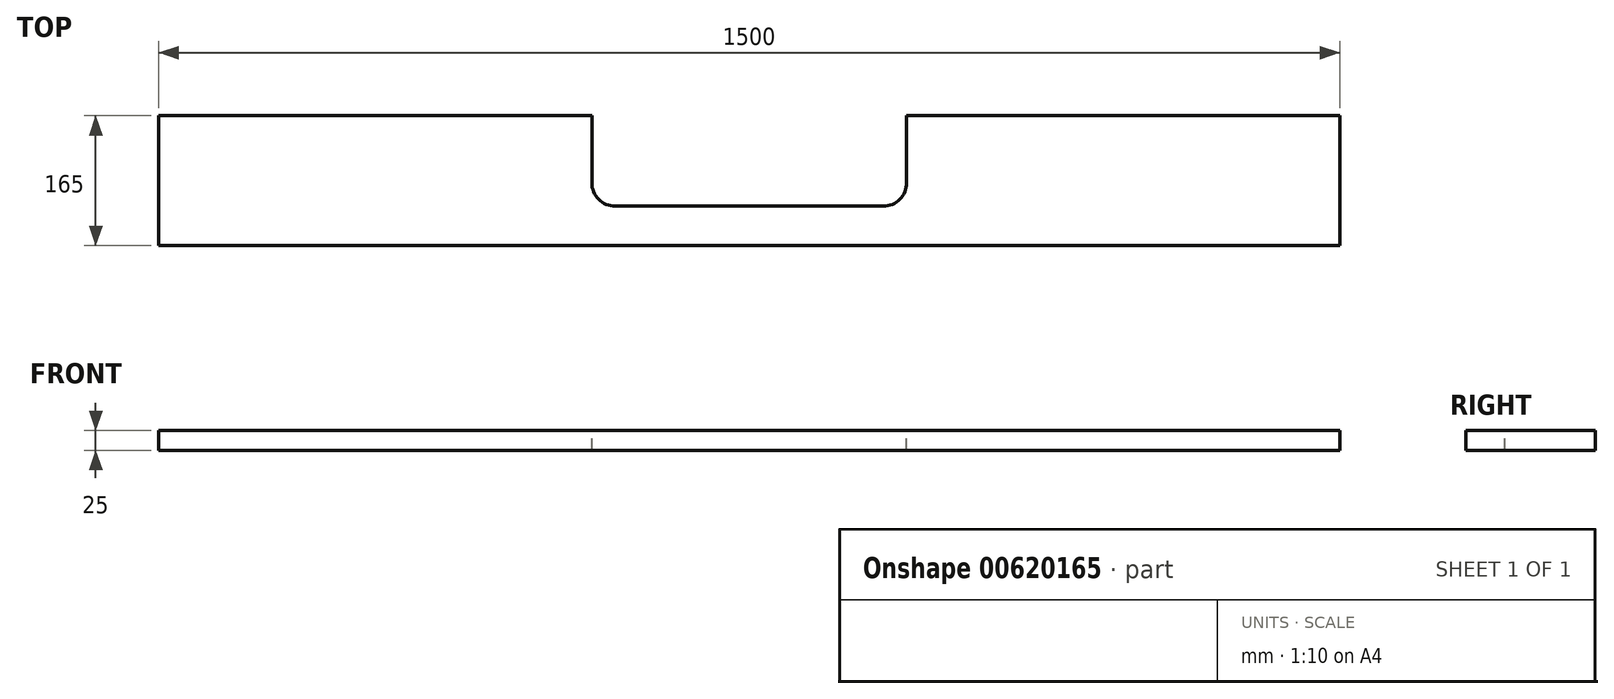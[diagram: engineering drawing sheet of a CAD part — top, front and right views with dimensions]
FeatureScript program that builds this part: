
annotation { "Feature Type Name" : "Feature", "Feature Type Description" : "" }
export const myFeature = defineFeature(function(context is Context, id is Id, definition is map)
    precondition{}
    {
        {
            var Q0;
            Q0=qCreatedBy(makeId("Top.planeOp"),FACE);
            var sketch = newSketch(context, id + "F0", { "sketchPlane" : qUnion([Q0])});
            skLineSegment(sketch, "E0.bottom", {"start": v(-750, 82.5) * mm, "end": v(750, 82.5) * mm});
            skLineSegment(sketch, "E0.top", {"start": v(-750, -82.5) * mm, "end": v(750, -82.5) * mm});
            skLineSegment(sketch, "E0.left", {"start": v(-750, 82.5) * mm, "end": v(-750, -82.5) * mm});
            skLineSegment(sketch, "E0.right", {"start": v(750, 82.5) * mm, "end": v(750, -82.5) * mm});
            skPoint(sketch, "E0.middle", {"position": v(0, 0) * mm});
            skSolve(sketch);
        }
        {
            var Q0;
            Q0=makeQuery(id+"F0.imprint","IMPRINT",FACE,{"disambiguationData":[TD([[makeQuery(id+"F0.imprint","IMPRINT",EDGE,{"derivedFrom":sQuery(id+"F0.wireOp",EDGE,"E0.bottom")}),-1.0]])]});
            extrude(context, id + "F1", {"entities" : qUnion([Q0]), "depth" : 25 * mm, "offsetDistance" : 25 * mm});
        }
        {
            var Q0;
            Q0=makeQuery(id+"F1.opExtrude","CAP_FACE",FACE,{"disambiguationData":[OSD([sQuery(id+"F0.wireOp",EDGE,"E0.bottom"),sQuery(id+"F0.wireOp",EDGE,"E0.top"),sQuery(id+"F0.wireOp",EDGE,"E0.left"),sQuery(id+"F0.wireOp",EDGE,"E0.right")])],"isStart":false});
            var sketch = newSketch(context, id + "F2", { "sketchPlane" : qUnion([Q0])});
            skLineSegment(sketch, "E1", {"start": v(-200, 82.5) * mm, "end": v(-200, -2.5) * mm});
            skLineSegment(sketch, "E2", {"start": v(-170, -32.5) * mm, "end": v(0, -32.5) * mm});
            skPoint(sketch, "E3.visualSharp", {"position": v(-200, -32.5) * mm});
            skArc(sketch, "E3.filletArc", {"start": v(-200, -2.5) * mm, "mid": v(-191.21, -23.71) * mm, "end": v(-170, -32.5) * mm});
            skLineSegment(sketch, "E4.MirrorCS", {"start": v(200, 82.5) * mm, "end": v(200, -2.5) * mm});
            skArc(sketch, "E5.MirrorCS", {"start": v(200, -2.5) * mm, "mid": v(191.21, -23.71) * mm, "end": v(170, -32.5) * mm});
            skLineSegment(sketch, "E6.MirrorCS", {"start": v(170, -32.5) * mm, "end": v(0, -32.5) * mm});
            skLineSegment(sketch, "E7", {"start": v(-200, 82.5) * mm, "end": v(200, 82.5) * mm});
            skSolve(sketch);
        }
        {
            var Q0;
            Q0=makeQuery(id+"F2.imprint","IMPRINT",FACE,{"disambiguationData":[TD([[makeQuery(id+"F2.imprint","IMPRINT",EDGE,{"derivedFrom":sQuery(id+"F2.wireOp",EDGE,"E1")}),1.0]])]});
            extrude(context, id + "F3", {"entities" : qUnion([Q0]), "operationType" : NewBodyOperationType.REMOVE, "endBound" : BoundingType.UP_TO_NEXT, "oppositeDirection" : true, "depth" : 25 * mm, "offsetDistance" : 25 * mm});
        }
    });
